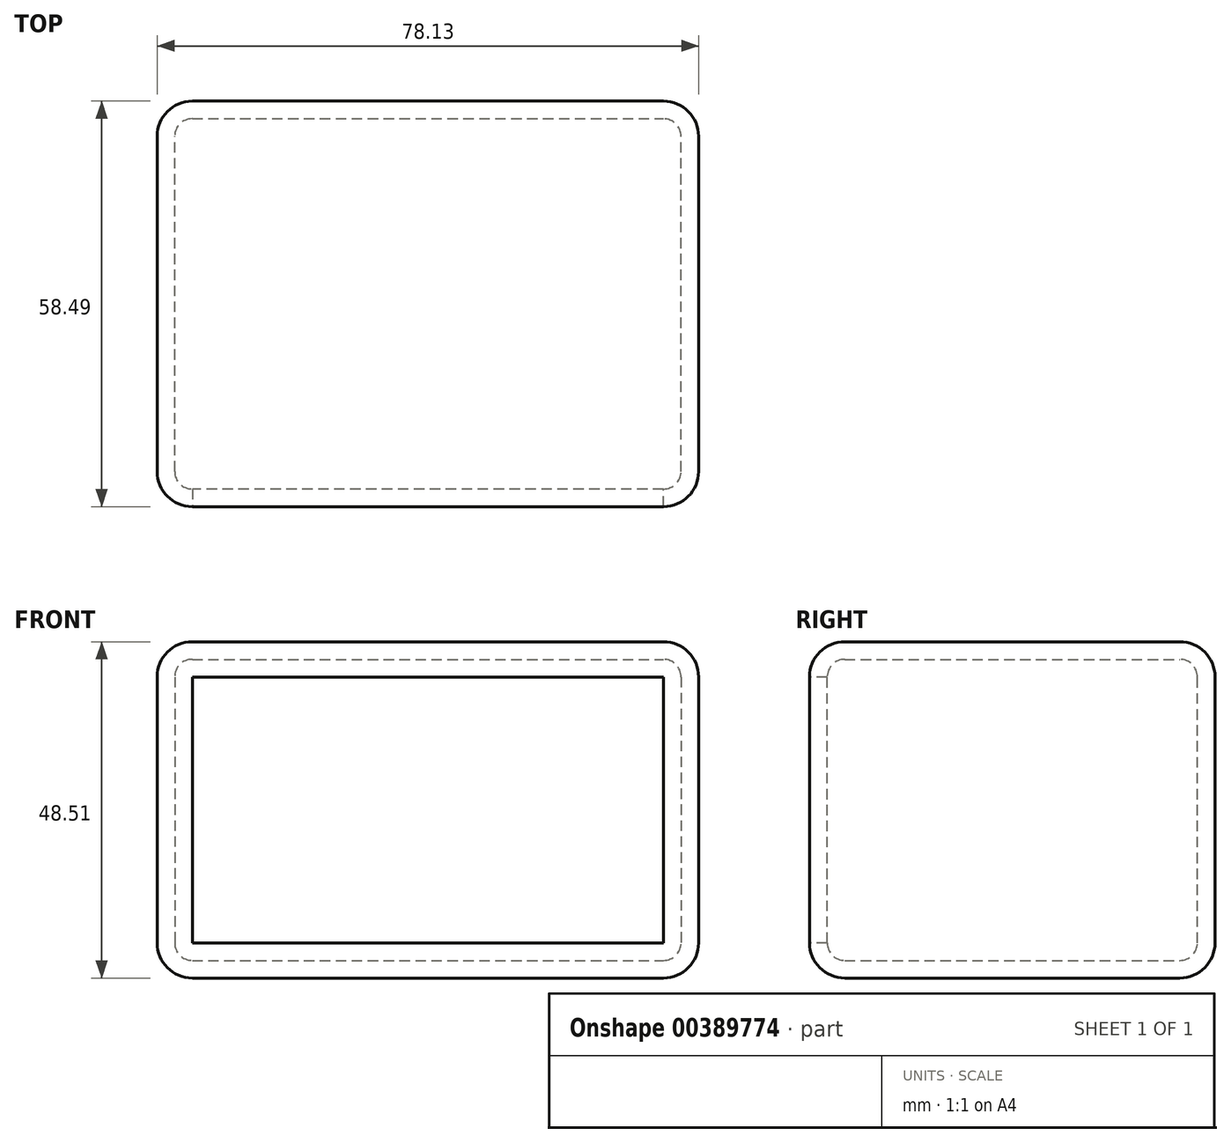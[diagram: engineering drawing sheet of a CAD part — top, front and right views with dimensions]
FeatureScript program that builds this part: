
annotation { "Feature Type Name" : "Feature", "Feature Type Description" : "" }
export const myFeature = defineFeature(function(context is Context, id is Id, definition is map)
    precondition{}
    {
        {
            var Q0;
            Q0=qCreatedBy(makeId("Top.planeOp"),FACE);
            var sketch = newSketch(context, id + "F0", { "sketchPlane" : qUnion([Q0])});
            skLineSegment(sketch, "E0.bottom", {"start": v(-45.48, 37.36) * mm, "end": v(32.65, 37.36) * mm});
            skLineSegment(sketch, "E0.top", {"start": v(-45.48, -21.13) * mm, "end": v(32.65, -21.13) * mm});
            skLineSegment(sketch, "E0.left", {"start": v(-45.48, 37.36) * mm, "end": v(-45.48, -21.13) * mm});
            skLineSegment(sketch, "E0.right", {"start": v(32.65, 37.36) * mm, "end": v(32.65, -21.13) * mm});
            skSolve(sketch);
        }
        {
            var Q0;
            Q0 = qSketchRegion(id + "F0", true);
            extrude(context, id + "F1", {"entities" : qUnion([Q0]), "depth" : 48.5 * mm});
        }
        {
            var Q0;
            Q0=makeQuery(id+"F1.opExtrude","CAP_EDGE",EDGE,{"disambiguationData":[OSD([sQuery(id+"F0.wireOp",EDGE,"E0.top")])],"isStart":false});
            var Q1;
            Q1=makeQuery(id+"F1.opExtrude","CAP_EDGE",EDGE,{"disambiguationData":[OSD([sQuery(id+"F0.wireOp",EDGE,"E0.left")])],"isStart":false});
            var Q2;
            Q2=makeQuery(id+"F1.opExtrude","CAP_EDGE",EDGE,{"disambiguationData":[OSD([sQuery(id+"F0.wireOp",EDGE,"E0.bottom")])],"isStart":false});
            var Q3;
            Q3=makeQuery(id+"F1.opExtrude","CAP_EDGE",EDGE,{"disambiguationData":[OSD([sQuery(id+"F0.wireOp",EDGE,"E0.right")])],"isStart":false});
            var Q4;
            Q4=makeQuery(id+"F1.opExtrude","SWEPT_EDGE",EDGE,{"disambiguationData":[OSD([sQuery(id+"F0.wireOp",EDGE,"E0.top"),sQuery(id+"F0.wireOp",EDGE,"E0.right")])]});
            var Q5;
            Q5=makeQuery(id+"F1.opExtrude","CAP_EDGE",EDGE,{"disambiguationData":[OSD([sQuery(id+"F0.wireOp",EDGE,"E0.right")])],"isStart":true});
            var Q6;
            Q6=makeQuery(id+"F1.opExtrude","SWEPT_EDGE",EDGE,{"disambiguationData":[OSD([sQuery(id+"F0.wireOp",EDGE,"E0.bottom"),sQuery(id+"F0.wireOp",EDGE,"E0.right")])]});
            var Q7;
            Q7=makeQuery(id+"F1.opExtrude","SWEPT_EDGE",EDGE,{"disambiguationData":[OSD([sQuery(id+"F0.wireOp",EDGE,"E0.top"),sQuery(id+"F0.wireOp",EDGE,"E0.left")])]});
            var Q8;
            Q8=makeQuery(id+"F1.opExtrude","SWEPT_EDGE",EDGE,{"disambiguationData":[OSD([sQuery(id+"F0.wireOp",EDGE,"E0.bottom"),sQuery(id+"F0.wireOp",EDGE,"E0.left")])]});
            var Q9;
            Q9=makeQuery(id+"F1.opExtrude","CAP_EDGE",EDGE,{"disambiguationData":[OSD([sQuery(id+"F0.wireOp",EDGE,"E0.left")])],"isStart":true});
            var Q10;
            Q10=makeQuery(id+"F1.opExtrude","CAP_EDGE",EDGE,{"disambiguationData":[OSD([sQuery(id+"F0.wireOp",EDGE,"E0.bottom")])],"isStart":true});
            fillet(context, id + "F2", {"entities" : qUnion([Q0, Q1, Q2, Q3, Q4, Q5, Q6, Q7, Q8, Q9, Q10]), "radius" : 5.08 * mm, "tangentPropagation" : true, "allowEdgeOverflow" : false});
        }
        {
            var Q0;
            Q0=makeQuery(id+"F1.opExtrude","CAP_EDGE",EDGE,{"disambiguationData":[OSD([sQuery(id+"F0.wireOp",EDGE,"E0.top")])],"isStart":true});
            fillet(context, id + "F3", {"entities" : qUnion([Q0]), "radius" : 5.08 * mm, "tangentPropagation" : true, "allowEdgeOverflow" : false});
        }
        {
            var Q0;
            Q0=makeQuery(id+"F1.opExtrude","SWEPT_FACE",FACE,{"disambiguationData":[OSD([sQuery(id+"F0.wireOp",EDGE,"E0.top")])]});
            shell(context, id + "F4", {"entities" : qUnion([Q0]), "thickness" : 2.54 * mm});
        }
    });
